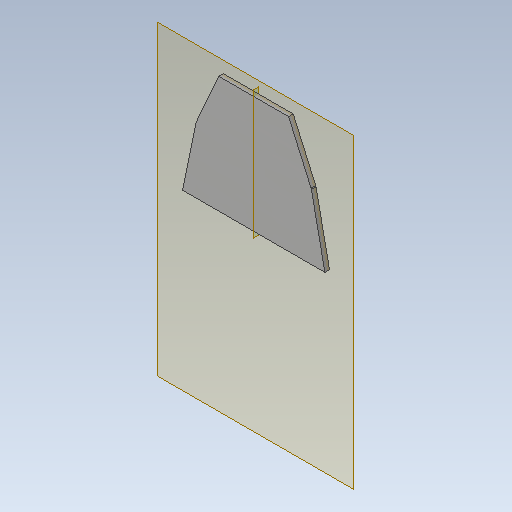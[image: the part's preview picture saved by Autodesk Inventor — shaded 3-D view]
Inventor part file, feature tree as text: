
AUTODESK INVENTOR PART (.ipt)
format: ipt  version: 2020.1 (Build 241239000, 239)  size: 174,080 bytes
history: native  units: mm
features: other x9, plane x1, sheet_metal_op x1, sketch x1, projected_geometry x1
ambient origin geometry x8: Origin, YZ Plane, XZ Plane, XY Plane, X Axis, Y Axis, Z Axis, Center Point
bodies: Solid1 (feature_tree)
feature tree (13):
  plane  "Work Plane1"
  sheet_metal_op  "Face1"
  other  "modplan parallel med plade"
  other  "midtplan"
  other  "Plate1"
  sketch  "Sketch3"  dims[d3=88.078826mm d4=44.039413mm d8=3.0mm d12=80.0mm d14=2.0mm d15=3.0mm d16=0.0mm]
  projected_geometry  "Projected Loop2"
  other  "2 mm mindre"
  other  "Definition1"
  parser-record x1  (decoder bookkeeping rows leaked as tree rows — omitted from the tree; the rows remain in map.json)
  other  "modul.iam"
  other  "stilladssøjle:1"
  other  "rør:1"
note: 1 file-system path scrubbed to <path> (originals preserved in map.json)
